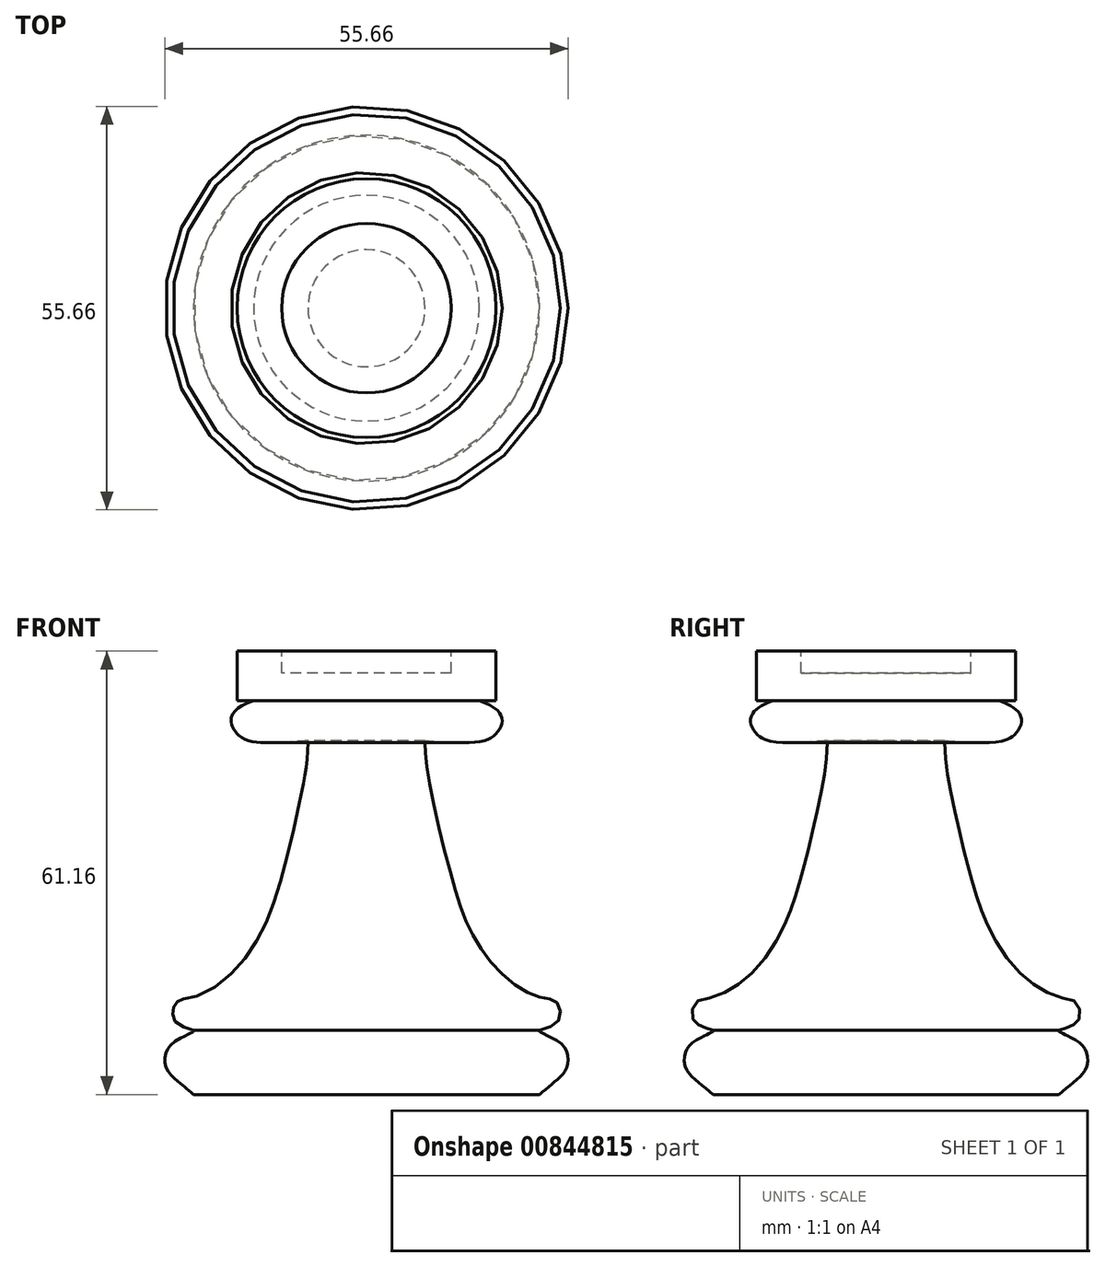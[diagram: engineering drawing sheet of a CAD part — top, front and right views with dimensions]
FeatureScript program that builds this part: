
annotation { "Feature Type Name" : "Feature", "Feature Type Description" : "" }
export const myFeature = defineFeature(function(context is Context, id is Id, definition is map)
    precondition{}
    {
        {
            var Q0;
            Q0=qCreatedBy(makeId("Front.planeOp"),FACE);
            var sketch = newSketch(context, id + "F0", { "sketchPlane" : qUnion([Q0])});
            skLineSegment(sketch, "E0", {"start": v(0, 50.53) * mm, "end": v(0, -41.64) * mm});
            skLineSegment(sketch, "E1", {"start": v(0, -41.64) * mm, "end": v(0, -30.76) * mm});
            skLineSegment(sketch, "E2", {"start": v(0, -30.76) * mm, "end": v(23.86, -30.76) * mm});
            skPoint(sketch, "E3.10.internal.orphan", {"position": v(23.86, -5.9) * mm});
            skPoint(sketch, "E3.11.internal.orphan", {"position": v(23.86, 29.85) * mm});
            skPoint(sketch, "E3.6.internal.orphan", {"position": v(23.86, -14.79) * mm});
            skFitSpline(sketch, "E4", {"points": [v(23.86, -30.76) * mm, v(26.04, -28.94) * mm, v(27.67, -26.95) * mm, v(26.95, -23.86) * mm, v(23.86, -22.05) * mm, v(23.86, -21.86) * mm], "startDerivative": vector(9.64, 7.96) * mm, "endDerivative": vector(1.43, 2.93) * mm});
            skFitSpline(sketch, "E5", {"points": [v(23.86, -21.86) * mm, v(26.58, -20.41) * mm, v(26.22, -18.05) * mm, v(23.86, -17.33) * mm, v(18.6, -14.06) * mm, v(14.24, -7.9) * mm, v(11.52, 0) * mm, v(8.44, 13.7) * mm, v(8.07, 18.05) * mm], "startDerivative": vector(37.15, 10.16) * mm, "endDerivative": vector(-0.84, 32.44) * mm});
            skPoint(sketch, "E6.8.internal.orphan", {"position": v(23.86, 31.66) * mm});
            skPoint(sketch, "E7.3.internal.orphan", {"position": v(23, 21.4) * mm});
            skPoint(sketch, "E8.5.internal.orphan", {"position": v(23.5, 20) * mm});
            skPoint(sketch, "E8.end.orphan", {"position": v(23, 20.08) * mm});
            skPoint(sketch, "E9.1.internal.orphan", {"position": v(25.83, 18.05) * mm});
            skPoint(sketch, "E10.end.orphan", {"position": v(23.5, 18.05) * mm});
            skFitSpline(sketch, "E11", {"points": [v(8.07, 18.05) * mm, v(16.23, 18.05) * mm, v(18.06, 19.29) * mm, v(18.71, 20.9) * mm, v(17.85, 22.42) * mm, v(15.58, 23.6) * mm], "startDerivative": vector(28.9, -2.13) * mm, "endDerivative": vector(-13.38, 5.45) * mm});
            skLineSegment(sketch, "E12", {"start": v(15.58, 23.6) * mm, "end": v(17.85, 23.6) * mm});
            skLineSegment(sketch, "E13", {"start": v(17.85, 23.6) * mm, "end": v(17.85, 30.4) * mm});
            skLineSegment(sketch, "E14", {"start": v(17.85, 30.4) * mm, "end": v(11.7, 30.4) * mm});
            skLineSegment(sketch, "E15", {"start": v(11.7, 30.4) * mm, "end": v(11.7, 27.38) * mm});
            skLineSegment(sketch, "E16", {"start": v(11.7, 27.38) * mm, "end": v(0, 27.38) * mm});
            skSolve(sketch);
        }
        {
            var Q0;
            Q0 = qSketchRegion(id + "F0", true);
            var Q1;
            Q1=sQuery(id+"F0.wireOp",EDGE,"E0");
            revolve(context, id + "F1", {"surfaceOperationType" : NewSurfaceOperationType.NEW, "entities" : qUnion([Q0]), "axis" : qUnion([Q1]), "revolveType" : RevolveType.FULL});
        }
    });
